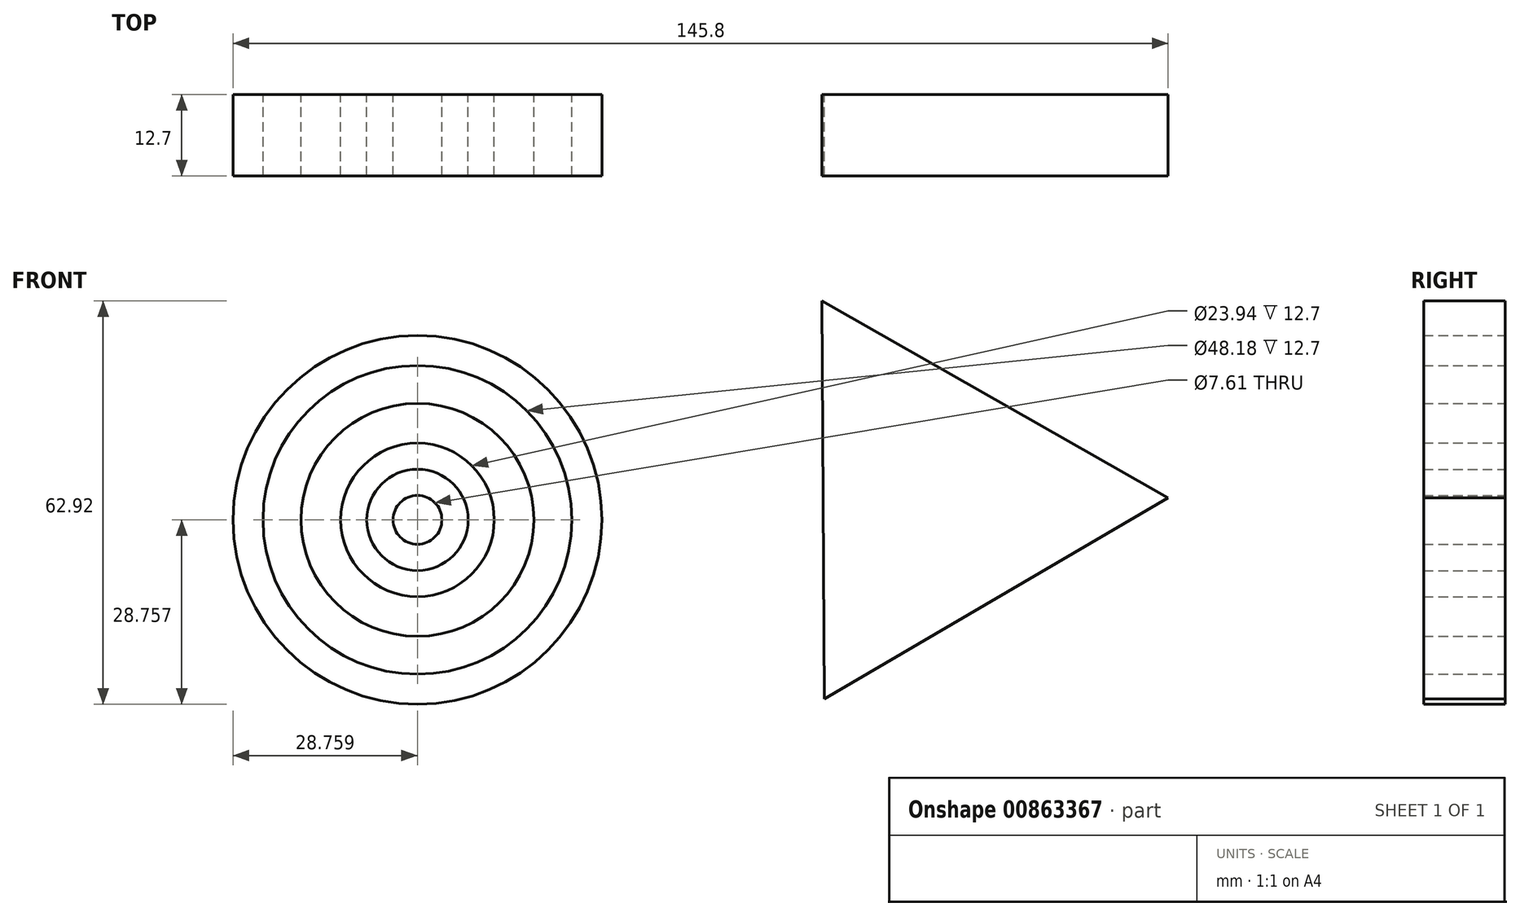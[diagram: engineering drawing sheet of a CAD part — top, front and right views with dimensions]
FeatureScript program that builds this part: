
annotation { "Feature Type Name" : "Feature", "Feature Type Description" : "" }
export const myFeature = defineFeature(function(context is Context, id is Id, definition is map)
    precondition{}
    {
        {
            var Q0;
            Q0=qCreatedBy(makeId("Front.planeOp"),FACE);
            var sketch = newSketch(context, id + "F0", { "sketchPlane" : qUnion([Q0])});
            skCircle(sketch, "E0", {"center": v(-40.15, 29.35) * mm, "radius": 28.76 * mm});
            skCircle(sketch, "E1", {"center": v(-40.15, 29.35) * mm, "radius": 24.09 * mm});
            skCircle(sketch, "E2", {"center": v(-40.15, 29.35) * mm, "radius": 18.16 * mm});
            skCircle(sketch, "E3", {"center": v(-40.15, 29.35) * mm, "radius": 11.97 * mm});
            skCircle(sketch, "E4", {"center": v(-40.15, 29.35) * mm, "radius": 7.9 * mm});
            skCircle(sketch, "E5", {"center": v(-40.15, 29.35) * mm, "radius": 3.8 * mm});
            skCircle(sketch, "E6", {"center": v(-40.15, 29.35) * mm, "radius": 1.85 * mm});
            skSolve(sketch);
        }
        {
            var Q0;
            Q0=qCreatedBy(makeId("Front.planeOp"),FACE);
            var sketch = newSketch(context, id + "F1", { "sketchPlane" : qUnion([Q0])});
            skCircle(sketch, "E7.cCircle", {"center": v(41.03, 32.56) * mm, "radius": 17.93 * mm, "construction": true});
            skLineSegment(sketch, "E7.0", {"start": v(76.89, 32.76) * mm, "end": v(23.27, 1.4) * mm});
            skLineSegment(sketch, "E7.1", {"start": v(23.27, 1.4) * mm, "end": v(22.92, 63.51) * mm});
            skLineSegment(sketch, "E7.2", {"start": v(22.92, 63.51) * mm, "end": v(76.89, 32.76) * mm});
            skPoint(sketch, "E7.0.midPoint", {"position": v(50.08, 17.08) * mm});
            skSolve(sketch);
        }
        {
            var Q0;
            Q0=makeQuery(id+"F0.imprint","IMPRINT",FACE,{"disambiguationData":[TD([[makeQuery(id+"F0.imprint","IMPRINT",EDGE,{"derivedFrom":sQuery(id+"F0.wireOp",EDGE,"E2")}),1.0]])]});
            var Q1;
            Q1=makeQuery(id+"F0.imprint","IMPRINT",FACE,{"disambiguationData":[TD([[makeQuery(id+"F0.imprint","IMPRINT",EDGE,{"derivedFrom":sQuery(id+"F0.wireOp",EDGE,"E0")}),1.0]])]});
            var Q2;
            Q2=makeQuery(id+"F0.imprint","IMPRINT",FACE,{"disambiguationData":[TD([[makeQuery(id+"F0.imprint","IMPRINT",EDGE,{"derivedFrom":sQuery(id+"F0.wireOp",EDGE,"E4")}),1.0]])]});
            extrude(context, id + "F2", {"entities" : qUnion([Q0, Q1, Q2]), "depth" : 12.7 * mm, "offsetDistance" : 25.4 * mm});
        }
        {
            var Q0;
            Q0=makeQuery(id+"F1.imprint","IMPRINT",FACE,{"disambiguationData":[TD([[makeQuery(id+"F1.imprint","IMPRINT",EDGE,{"derivedFrom":sQuery(id+"F1.wireOp",EDGE,"E7.0")}),-1.0]])]});
            extrude(context, id + "F3", {"entities" : qUnion([Q0]), "depth" : 12.7 * mm, "offsetDistance" : 25.4 * mm});
        }
    });
